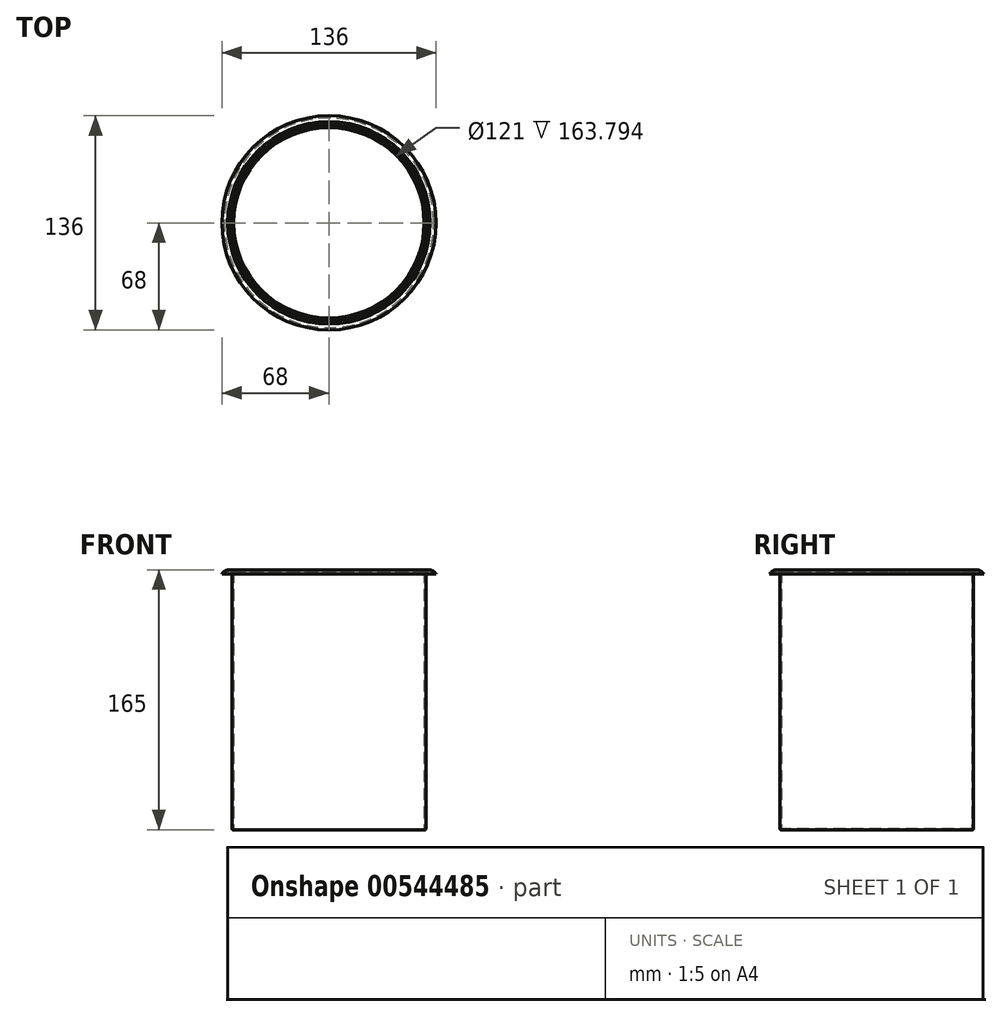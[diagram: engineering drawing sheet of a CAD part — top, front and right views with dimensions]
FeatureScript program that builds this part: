
annotation { "Feature Type Name" : "Feature", "Feature Type Description" : "" }
export const myFeature = defineFeature(function(context is Context, id is Id, definition is map)
    precondition{}
    {
        {
            var Q0;
            Q0=qCreatedBy(makeId("Front.planeOp"),FACE);
            var sketch = newSketch(context, id + "F0", { "sketchPlane" : qUnion([Q0])});
            skLineSegment(sketch, "E0.bottom", {"start": v(-1, 0) * mm, "end": v(-61.5, 0) * mm});
            skLineSegment(sketch, "E0.right", {"start": v(-61.5, 0.5) * mm, "end": v(-61.5, 164.3) * mm});
            skLineSegment(sketch, "E1", {"start": v(-63.44, 165) * mm, "end": v(-65.25, 165) * mm});
            skArc(sketch, "E2", {"start": v(-61.5, 164.3) * mm, "mid": v(-62.44, 164.74) * mm, "end": v(-63.44, 165) * mm});
            skPoint(sketch, "E2.first.point", {"position": v(-65.25, 165) * mm});
            skPoint(sketch, "E2.second.point", {"position": v(-65.25, 154) * mm});
            skPoint(sketch, "E2.second.point.positionSnap0", {"position": v(-65.25, 165) * mm});
            skPoint(sketch, "E2.third.point", {"position": v(-61.5, 164.3) * mm});
            skArc(sketch, "E3.trimOffspring", {"start": v(-62.5, 163.77) * mm, "mid": v(-65.26, 164.18) * mm, "end": v(-67.53, 162.57) * mm});
            skLineSegment(sketch, "E4", {"start": v(-69, 162.57) * mm, "end": v(-67.53, 162.57) * mm});
            skLineSegment(sketch, "E5", {"start": v(-62.5, 163.77) * mm, "end": v(-62.5, 162.92) * mm});
            skLineSegment(sketch, "E6", {"start": v(-61.5, 0) * mm, "end": v(-62, 0) * mm});
            skLineSegment(sketch, "E7", {"start": v(-62.5, 0.5) * mm, "end": v(-62.5, 162.92) * mm});
            skPoint(sketch, "E8.visualSharp", {"position": v(-62.5, 0) * mm});
            skArc(sketch, "E8.filletArc", {"start": v(-62.5, 0.5) * mm, "mid": v(-62.35, 0.15) * mm, "end": v(-62, 0) * mm});
            skPoint(sketch, "E9.orphan", {"position": v(-61.5, 165) * mm});
            skArc(sketch, "E10.trimOffspring", {"start": v(-65.25, 165) * mm, "mid": v(-67.38, 164.18) * mm, "end": v(-69, 162.57) * mm});
            skPoint(sketch, "E11.orphan", {"position": v(-69, 165) * mm});
            skLineSegment(sketch, "E12.trimOffspring", {"start": v(-61.5, 0.5) * mm, "end": v(-1, 0.5) * mm});
            skLineSegment(sketch, "E13", {"start": v(-1, 0.25) * mm, "end": v(-1, 35.18) * mm, "construction": true});
            skLineSegment(sketch, "E14", {"start": v(-1, 0.5) * mm, "end": v(-1, 0) * mm});
            skLineSegment(sketch, "E15", {"start": v(-1, 0.5) * mm, "end": v(-1, 0) * mm, "construction": true});
            skSolve(sketch);
        }
        {
            var Q0;
            Q0=makeQuery(id+"F0.imprint","IMPRINT",FACE,{"disambiguationData":[TD([[makeQuery(id+"F0.imprint","IMPRINT",EDGE,{"derivedFrom":sQuery(id+"F0.wireOp",EDGE,"E0.bottom")}),-1.0]])]});
            var Q1;
            Q1=sQuery(id+"F0.wireOp",EDGE,"E13");
            revolve(context, id + "F1", {"entities" : qUnion([Q0]), "axis" : qUnion([Q1]), "revolveType" : RevolveType.FULL});
        }
    });
